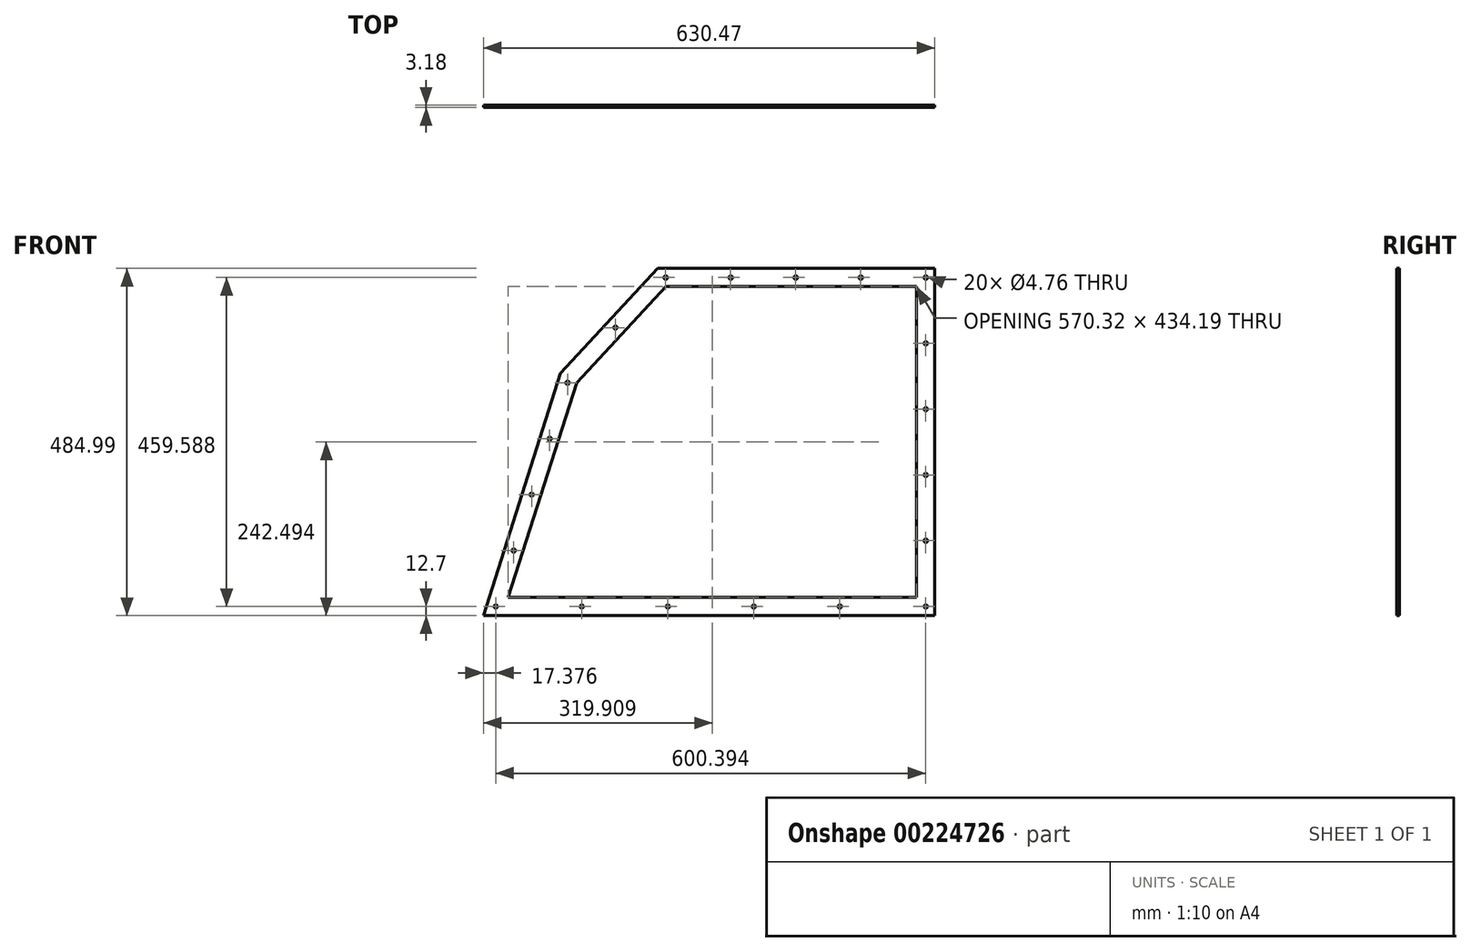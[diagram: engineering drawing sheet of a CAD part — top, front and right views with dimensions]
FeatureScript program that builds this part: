
annotation { "Feature Type Name" : "Feature", "Feature Type Description" : "" }
export const myFeature = defineFeature(function(context is Context, id is Id, definition is map)
    precondition{}
    {
        {
            var Q0;
            Q0=qCreatedBy(makeId("Front.planeOp"),FACE);
            var sketch = newSketch(context, id + "F0", { "sketchPlane" : qUnion([Q0])});
            skLineSegment(sketch, "E0", {"start": v(-630.47, 0) * mm, "end": v(0, 0) * mm});
            skLineSegment(sketch, "E1", {"start": v(0, 0) * mm, "end": v(0, 484.99) * mm});
            skLineSegment(sketch, "E2", {"start": v(0, 484.99) * mm, "end": v(-386.69, 484.99) * mm});
            skLineSegment(sketch, "E3", {"start": v(-386.69, 484.99) * mm, "end": v(-522.69, 338.45) * mm});
            skLineSegment(sketch, "E4", {"start": v(-522.69, 338.45) * mm, "end": v(-630.47, 0) * mm});
            skLineSegment(sketch, "E5.0", {"start": v(-500.2, 325.33) * mm, "end": v(-595.72, 25.4) * mm});
            skLineSegment(sketch, "E5.1", {"start": v(-375.6, 459.59) * mm, "end": v(-500.2, 325.33) * mm});
            skLineSegment(sketch, "E5.2", {"start": v(-595.72, 25.4) * mm, "end": v(-25.4, 25.4) * mm});
            skLineSegment(sketch, "E5.3", {"start": v(-25.4, 25.4) * mm, "end": v(-25.4, 459.59) * mm});
            skLineSegment(sketch, "E5.4", {"start": v(-25.4, 459.59) * mm, "end": v(-375.6, 459.59) * mm});
            skSolve(sketch);
        }
        {
            var Q0;
            Q0=qSketchRegion(id+"F0",true);
            extrude(context, id + "F1", {"entities" : qUnion([Q0]), "depth" : 1.59 * mm, "hasSecondDirection" : true, "secondDirectionOppositeDirection" : true, "secondDirectionDepth" : 1.59 * mm});
        }
        {
            var Q0;
            Q0=makeQuery(id+"F1.opExtrude","CAP_FACE",FACE,{"disambiguationData":[OSD([sQuery(id+"F0.wireOp",EDGE,"E0"),sQuery(id+"F0.wireOp",EDGE,"E1"),sQuery(id+"F0.wireOp",EDGE,"E2"),sQuery(id+"F0.wireOp",EDGE,"E3"),sQuery(id+"F0.wireOp",EDGE,"E4"),sQuery(id+"F0.wireOp",EDGE,"E5.0"),sQuery(id+"F0.wireOp",EDGE,"E5.1"),sQuery(id+"F0.wireOp",EDGE,"E5.2"),sQuery(id+"F0.wireOp",EDGE,"E5.3"),sQuery(id+"F0.wireOp",EDGE,"E5.4")])],"isStart":false});
            var sketch = newSketch(context, id + "F2", { "sketchPlane" : qUnion([Q0])});
            skCircle(sketch, "E6", {"center": v(-12.7, 12.7) * mm, "radius": 2.38 * mm});
            skCircle(sketch, "E7", {"center": v(-12.7, 472.29) * mm, "radius": 2.38 * mm});
            skCircle(sketch, "E8", {"center": v(-375.92, 472.29) * mm, "radius": 2.38 * mm});
            skCircle(sketch, "E9", {"center": v(-512.9, 325.33) * mm, "radius": 2.38 * mm});
            skCircle(sketch, "E10", {"center": v(-613.1, 12.7) * mm, "radius": 2.38 * mm});
            skCircle(sketch, "E11.1.0.0", {"center": v(-493.01, 12.7) * mm, "radius": 2.38 * mm});
            skCircle(sketch, "E11.2.0.0", {"center": v(-372.93, 12.7) * mm, "radius": 2.38 * mm});
            skCircle(sketch, "E11.3.0.0", {"center": v(-252.85, 12.7) * mm, "radius": 2.38 * mm});
            skCircle(sketch, "E11.4.0.0", {"center": v(-132.77, 12.7) * mm, "radius": 2.38 * mm});
            skLineSegment(sketch, "E11.direction1", {"start": v(-613.1, 12.7) * mm, "end": v(-493.01, 12.7) * mm, "construction": true});
            skLineSegment(sketch, "E12", {"start": v(-512.9, 325.33) * mm, "end": v(-613.1, 12.7) * mm, "construction": true});
            skCircle(sketch, "E13", {"center": v(-537.95, 247.18) * mm, "radius": 2.38 * mm});
            skCircle(sketch, "E14", {"center": v(-563, 169.02) * mm, "radius": 2.38 * mm});
            skCircle(sketch, "E15", {"center": v(-588.05, 90.86) * mm, "radius": 2.38 * mm});
            skLineSegment(sketch, "E16", {"start": v(-386.69, 466.32) * mm, "end": v(-505.36, 338.45) * mm, "construction": true});
            skCircle(sketch, "E17", {"center": v(-446.02, 402.38) * mm, "radius": 2.38 * mm});
            skCircle(sketch, "E18.1.0.0", {"center": v(-285.11, 472.29) * mm, "radius": 2.38 * mm});
            skCircle(sketch, "E18.2.0.0", {"center": v(-194.3, 472.29) * mm, "radius": 2.38 * mm});
            skCircle(sketch, "E18.3.0.0", {"center": v(-103.5, 472.29) * mm, "radius": 2.38 * mm});
            skLineSegment(sketch, "E18.direction1", {"start": v(-375.92, 472.29) * mm, "end": v(-285.11, 472.29) * mm, "construction": true});
            skCircle(sketch, "E19.0.1.0", {"center": v(-12.7, 380.37) * mm, "radius": 2.38 * mm});
            skCircle(sketch, "E19.0.2.0", {"center": v(-12.7, 288.45) * mm, "radius": 2.38 * mm});
            skCircle(sketch, "E19.0.3.0", {"center": v(-12.7, 196.54) * mm, "radius": 2.38 * mm});
            skCircle(sketch, "E19.0.4.0", {"center": v(-12.7, 104.62) * mm, "radius": 2.38 * mm});
            skLineSegment(sketch, "E19.direction1", {"start": v(-12.7, 472.29) * mm, "end": v(12.7, 472.29) * mm, "construction": true});
            skLineSegment(sketch, "E19.direction2", {"start": v(-12.7, 472.29) * mm, "end": v(-12.7, 380.37) * mm, "construction": true});
            skSolve(sketch);
        }
        {
            var Q0;
            Q0=qSketchRegion(id+"F2",true);
            var Q1;
            Q1=makeQuery(id+"F1.opExtrude","CAP_FACE",FACE,{"disambiguationData":[OSD([sQuery(id+"F0.wireOp",EDGE,"E0"),sQuery(id+"F0.wireOp",EDGE,"E1"),sQuery(id+"F0.wireOp",EDGE,"E2"),sQuery(id+"F0.wireOp",EDGE,"E3"),sQuery(id+"F0.wireOp",EDGE,"E4"),sQuery(id+"F0.wireOp",EDGE,"E5.0"),sQuery(id+"F0.wireOp",EDGE,"E5.1"),sQuery(id+"F0.wireOp",EDGE,"E5.2"),sQuery(id+"F0.wireOp",EDGE,"E5.3"),sQuery(id+"F0.wireOp",EDGE,"E5.4")])],"isStart":true});
            extrude(context, id + "F3", {"entities" : qUnion([Q0]), "operationType" : NewBodyOperationType.REMOVE, "endBound" : BoundingType.UP_TO_SURFACE, "oppositeDirection" : true, "endBoundEntityFace" : qUnion([Q1]), "depth" : 25.4 * mm});
        }
    });
